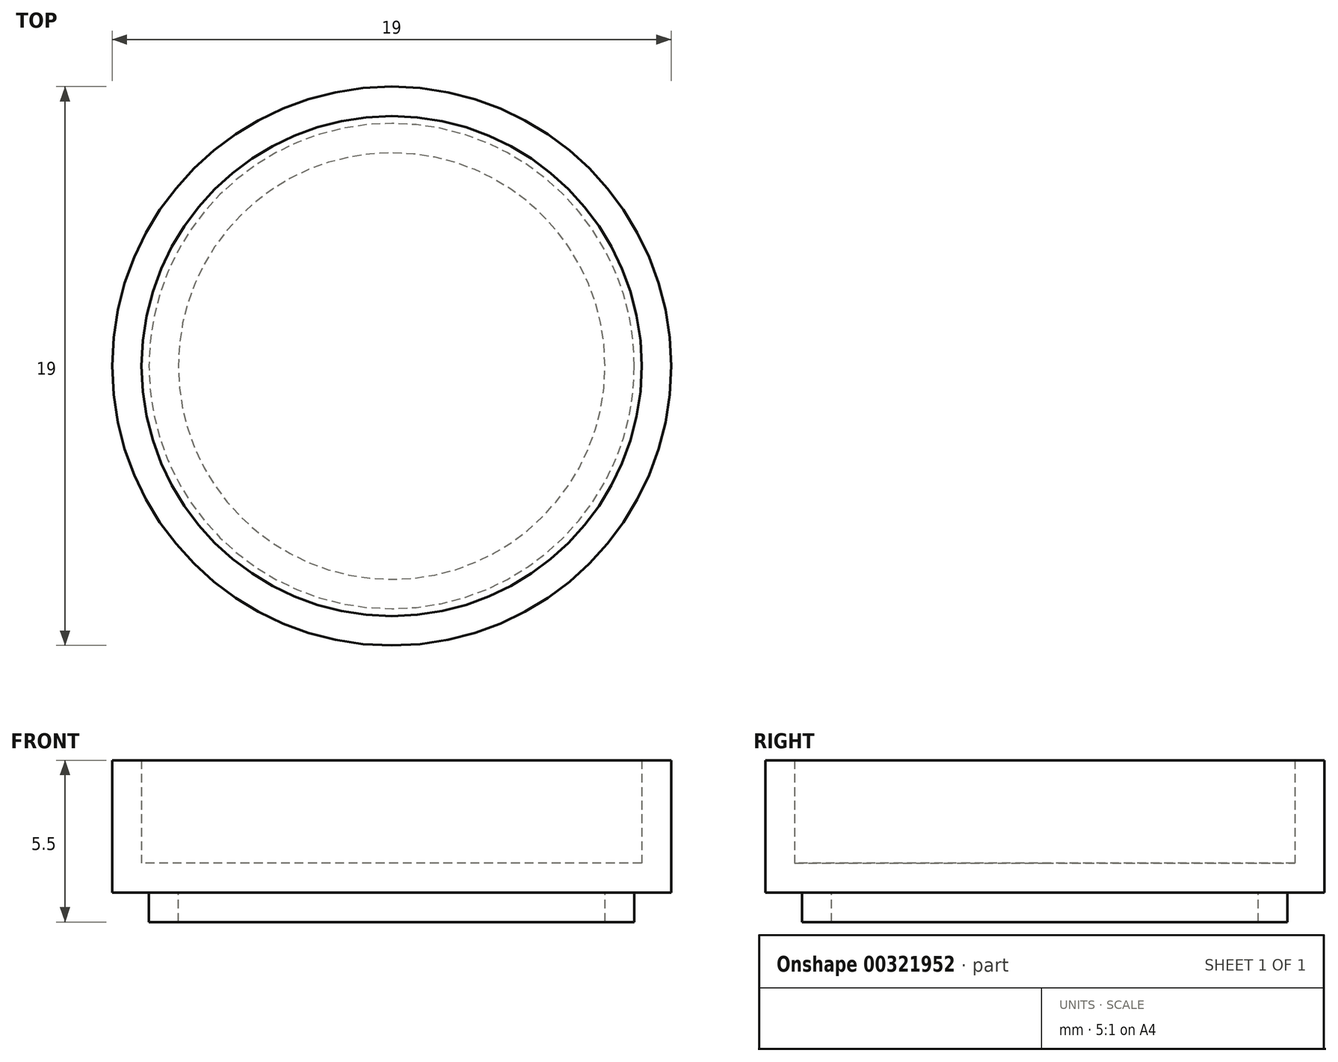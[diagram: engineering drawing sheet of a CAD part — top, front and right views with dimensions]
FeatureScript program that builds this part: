
annotation { "Feature Type Name" : "Feature", "Feature Type Description" : "" }
export const myFeature = defineFeature(function(context is Context, id is Id, definition is map)
    precondition{}
    {
        {
            var Q0;
            Q0=qCreatedBy(makeId("Top.planeOp"),FACE);
            var sketch = newSketch(context, id + "F0", { "sketchPlane" : qUnion([Q0])});
            skCircle(sketch, "E0", {"center": v(0, 0) * mm, "radius": 8.5 * mm});
            skCircle(sketch, "E1", {"center": v(0, 0) * mm, "radius": 9.5 * mm});
            skCircle(sketch, "E2", {"center": v(0, 0) * mm, "radius": 8.25 * mm});
            skCircle(sketch, "E3", {"center": v(0, 0) * mm, "radius": 7.25 * mm});
            skSolve(sketch);
        }
        {
            var Q0;
            Q0=makeQuery(id+"F0.imprint","IMPRINT",FACE,{"disambiguationData":[TD([[makeQuery(id+"F0.imprint","IMPRINT",EDGE,{"derivedFrom":sQuery(id+"F0.wireOp",EDGE,"E0")}),-1.0]])]});
            extrude(context, id + "F1", {"entities" : qUnion([Q0]), "depth" : 3.5 * mm});
        }
        {
            var Q0;
            Q0=makeQuery(id+"F0.imprint","IMPRINT",FACE,{"disambiguationData":[TD([[makeQuery(id+"F0.imprint","IMPRINT",EDGE,{"derivedFrom":sQuery(id+"F0.wireOp",EDGE,"E0")}),1.0]])]});
            var Q1;
            Q1=makeQuery(id+"F0.imprint","IMPRINT",FACE,{"disambiguationData":[TD([[makeQuery(id+"F0.imprint","IMPRINT",EDGE,{"derivedFrom":sQuery(id+"F0.wireOp",EDGE,"E0")}),-1.0]])]});
            var Q2;
            Q2=makeQuery(id+"F0.imprint","IMPRINT",FACE,{"disambiguationData":[TD([[makeQuery(id+"F0.imprint","IMPRINT",EDGE,{"derivedFrom":sQuery(id+"F0.wireOp",EDGE,"E2")}),1.0]])]});
            var Q3;
            Q3=makeQuery(id+"F0.imprint","IMPRINT",FACE,{"disambiguationData":[TD([[makeQuery(id+"F0.imprint","IMPRINT",EDGE,{"derivedFrom":sQuery(id+"F0.wireOp",EDGE,"E3")}),1.0]])]});
            extrude(context, id + "F2", {"entities" : qUnion([Q0, Q1, Q2, Q3]), "operationType" : NewBodyOperationType.ADD, "oppositeDirection" : true, "depth" : 1 * mm});
        }
        {
            var Q0;
            Q0=makeQuery(id+"F0.imprint","IMPRINT",FACE,{"disambiguationData":[TD([[makeQuery(id+"F0.imprint","IMPRINT",EDGE,{"derivedFrom":sQuery(id+"F0.wireOp",EDGE,"E2")}),1.0]])]});
            extrude(context, id + "F3", {"entities" : qUnion([Q0]), "operationType" : NewBodyOperationType.ADD, "oppositeDirection" : true, "depth" : 2 * mm});
        }
    });
